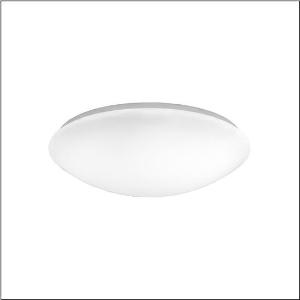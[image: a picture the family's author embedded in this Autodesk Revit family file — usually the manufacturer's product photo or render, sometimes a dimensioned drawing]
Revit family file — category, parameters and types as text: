
# Revit family: round_31_b_5pja230001a
name_source: partatom
category: Lighting Fixtures
units: mm (PartAtom-declared; Revit-internal decimal feet)

## family parameters
Cut with Voids When Loaded = No
Host = Face
Light Source = No
Part Type = Normal
Room Calculation Point = No
Round Connector Dimension = Use Diameter
Shared = No

## types (1)
- --- (1 x LED, 4900 lm, 39 W, 4000K)
    Apparent Load = 39 VA
    CIE Flux Codes = 42 71 89 88 100
    Color Rendering = 80
    Color Temperature = 4000K
    Default Elevation = 1800 mm
    Description = Round 31 B, wall and ceiling luminaire, primary optical cover: enclosure, of PMMA, light emission: direct distribution, primary light characteristic: symmetric, installation type: surface-mounted, LED, rated luminous flux: 4.900lm, luminous efficacy: 126lm/W, light colour: 840, colour temperature: 4000K, with terminal, 3-pole, max. 2.5mm², mains connection: 230V, AC, 50/60Hz, rated input power: 39W, luminaire housing, round, of steel, white, diameter: 464mm, height: 120mm, protection rating (complete): IP40, insulation class (complete): insulation class I (protective earthing), certification: CE, impact resistance: IK02, packaging unit: 1 piece
    Height = 120 mm
    Lamp = 1 x LED
    Lamp Light Flux = 4900 lm
    Lamp Power = 39 W
    Lamp count = 1
    Length = 464 mm
    Luminous efficacy = 126 lm/W
    Manufacturer = Siteco
    ModVariant = No
    Model = 5PJA230001A
    Mounting Place = Ceiling
    Mounting Type = Surface mounted
    Number of Poles = 1
    OnlyDefault = Yes
    Power Factor = 1
    Product Name = Round 31 B
    Product group = wall and ceiling luminaire
    ProductGroupID = 302
    Protection Class = Protection class I
    Protection Degree = IP 40
    RLX_Detail_Level = 1
    RLX_Emergency_Light_Flux = 0 lm
    RLX_Emergency_Type = 0
    RLX_Emergency_Type_DB = No
    RlxData = <blob elided: 13749 chars, md5=f34e5f29>
    Socket = socket
    Standby Power = 0 W
    System Light Flux = 4900 lm
    System Power = 39 W
    Type Comments = factory setting: luminous flux: 100 % | (ON | ON | ON) | 1050 mA
    Type Image = l_1258313.jpg
    URL = http://relux.com
    VarID = @adj_032351
    Voltage = 0 V
    Weight = 0.00 kg
    Width = 0 mm  [stored 0 ft]

note: [stored X ft] marks values corroborated as IEEE doubles in the binary element streams (Revit-internal decimal feet)

## geometry (parser evidence)
native form markers: Sweep x12
no freeform markers — native parametric forms only
